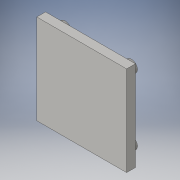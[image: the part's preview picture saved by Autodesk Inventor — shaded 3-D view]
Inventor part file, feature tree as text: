
AUTODESK INVENTOR PART (.ipt)
format: ipt  version: 2016 (Build 200138000, 138)  size: 121,344 bytes
history: native  units: mm
features: sketch x3, extrude x2, hole x1
ambient origin geometry x8: Origin, YZ Plane, XZ Plane, XY Plane, X Axis, Y Axis, Z Axis, Center Point
bodies: Solid1 (feature_tree)
feature tree (6):
  extrude  "Extrusion1"  Depth=46.0mm
  extrude  "Extrusion2"  Depth=4.5mm
  hole  "Hole1"  [1 undecoded]
  sketch  "Sketch1"  dims[d0=46.0mm d1=46.0mm]
  sketch  "Sketch2"  dims[d2=4.5mm d3=0.0mm d4=6.1mm]
  sketch  "Sketch3"  dims[d5=6.0mm d6=6.0mm d7=6.1mm d8=6.0mm d9=6.0mm d10=6.1mm d11=6.0mm d12=6.0mm d13=6.1mm d14=4.0mm d15=0.0mm d16=6.0mm d17=6.0mm d18=24.0mm d19=24.0mm d20=6.0mm d21=4.0mm d22=2.0mm d23=90.0deg d24=1.5mm d25=0.0mm]
note: 1 required parameter value undecoded (feature->parameter linkage not recoverable at this tier; creation-order binding heuristic only, values carry confidence <= 0.55)
